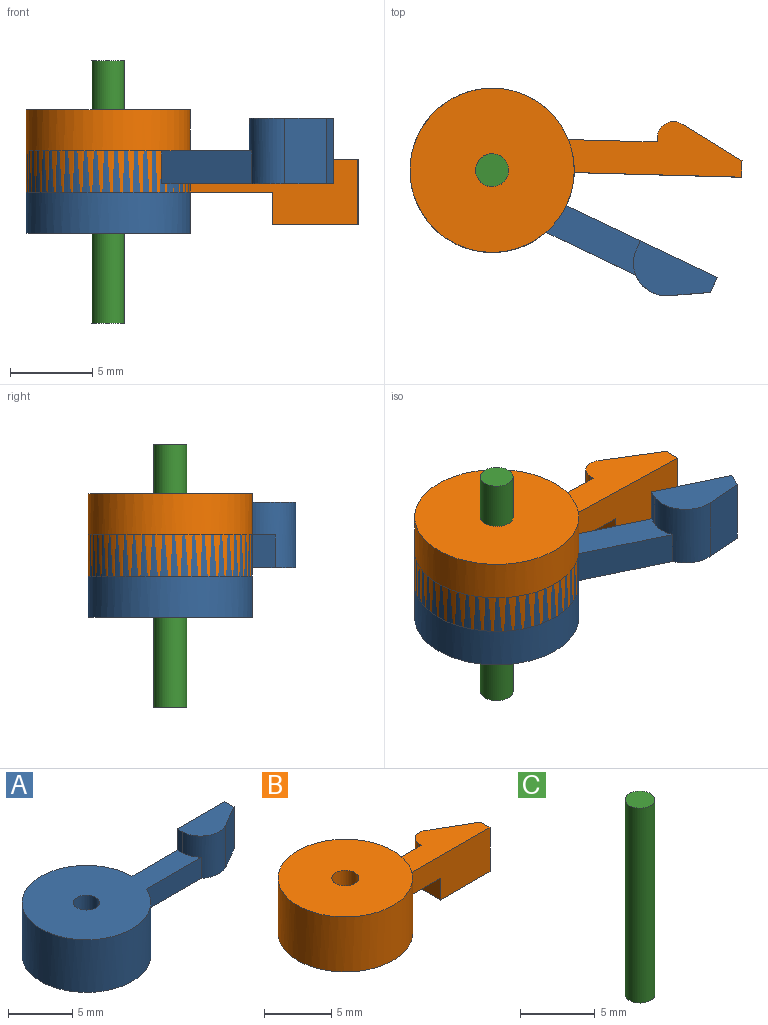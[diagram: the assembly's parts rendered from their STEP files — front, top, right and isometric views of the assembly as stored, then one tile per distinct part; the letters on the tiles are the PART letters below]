
ASSEMBLY  parts=3 mates=2
PART A: 12 faces, bbox 20.2x10x7 mm
  f0: cylinder r=5mm len=10mm, axis (0,0,1), area 153mm2, adj f1,f2,f3,f4,f5
  f1: plane 10x10mm, normal (0,0,-1), area 75.4mm2, adj f0,f11
  f2: plane 15.64x10mm, normal (0,0,1), area 86mm2, adj f0,f3,f4,f6,f10,f11
  f3: plane 10.2x4mm, normal (0,1,0), area 30.8mm2, adj f0,f2,f5,f6,f8,f9
  f4: plane 6.06x2mm, normal (0,-1,0), area 12.1mm2, adj f0,f2,f5,f10
  f5: plane 10.61x2.54mm, normal (0,0,-1), area 20.8mm2, adj f0,f3,f4,f7,f8,f10
  f6: plane 2x0.54mm, normal (-1,0,0), area 1.1mm2, adj f2,f3,f9,f10
  f7: plane 4x2.2mm, normal (0.5,-0.87,0), area 10.1mm2, adj f5,f8,f9,f10
  f8: plane 4x1mm, normal (1,0,0), area 4mm2, adj f3,f5,f7,f9
  f9: plane 5.2x2.54mm, normal (0,0,1), area 10.3mm2, adj f3,f6,f7,f8,f10
  f10: cylinder r=2mm len=4mm, axis (0,0,1), area 13.5mm2, adj f2,f4,f5,f6,f7,f9
  f11: cylinder r=1mm len=5mm, axis (0,0,1), area 31.4mm2, adj f1,f2
PART B: 12 faces, bbox 20.2x10x7 mm
  f0: cylinder r=5mm len=10mm, axis (0,0,-1), area 153mm2, adj f1,f2,f3,f4,f5
  f1: plane 10x10mm, normal (0,0,1), area 75.4mm2, adj f0,f11
  f2: plane 15x10mm, normal (0,0,-1), area 85.7mm2, adj f0,f3,f4,f8,f11
  f3: plane 10.2x4mm, normal (0,-1,0), area 30.8mm2, adj f0,f2,f5,f6,f8,f9
  f4: plane 5.42x2mm, normal (0,1,0), area 10.8mm2, adj f0,f2,f5,f8
  f5: plane 10.61x3.27mm, normal (0,0,1), area 22.6mm2, adj f0,f3,f4,f6,f7,f8,f10
  f6: plane 4x1mm, normal (1,0,0), area 4mm2, adj f3,f5,f7,f9
  f7: plane 4x3.7mm, normal (0.5,0.87,0), area 17.1mm2, adj f5,f6,f9,f10
  f8: plane 4x2.27mm, normal (-1,0,0), area 5.1mm2, adj f2,f3,f4,f5,f9,f10
  f9: plane 5.2x3.27mm, normal (0,0,-1), area 12.3mm2, adj f3,f6,f7,f8,f10
  f10: cylinder r=1mm len=4mm, axis (0,0,-1), area 8.4mm2, adj f5,f7,f8,f9
  f11: cylinder r=1mm len=5mm, axis (0,0,-1), area 31.4mm2, adj f1,f2
PART C: 3 faces, bbox 2x2x16 mm
  f0: cylinder r=1mm len=16mm, axis (0,0,-1), area 100.5mm2, adj f1,f2
  f1: plane 2x2mm, normal (0,0,1), area 3.1mm2, adj f0
  f2: plane 2x2mm, normal (0,0,-1), area 3.1mm2, adj f0
PLACE A rot(axis=(0,0,-1),25.5deg) t=(-16.68,-8.57,2.97)mm
PLACE B rot(axis=(0,0,-1),1.6deg) t=(-16.68,-8.57,0.47)mm
PLACE C t=(-16.68,-8.57,0.47)mm fixed
MATE revolute A.f0 <-> B.f0  axis (0,0,1) through (-16.68,-8.57,2.97)mm
MATE revolute C.f0 <-> A.f0  axis (0,0,-1) through (-16.68,-8.57,0.47)mm
